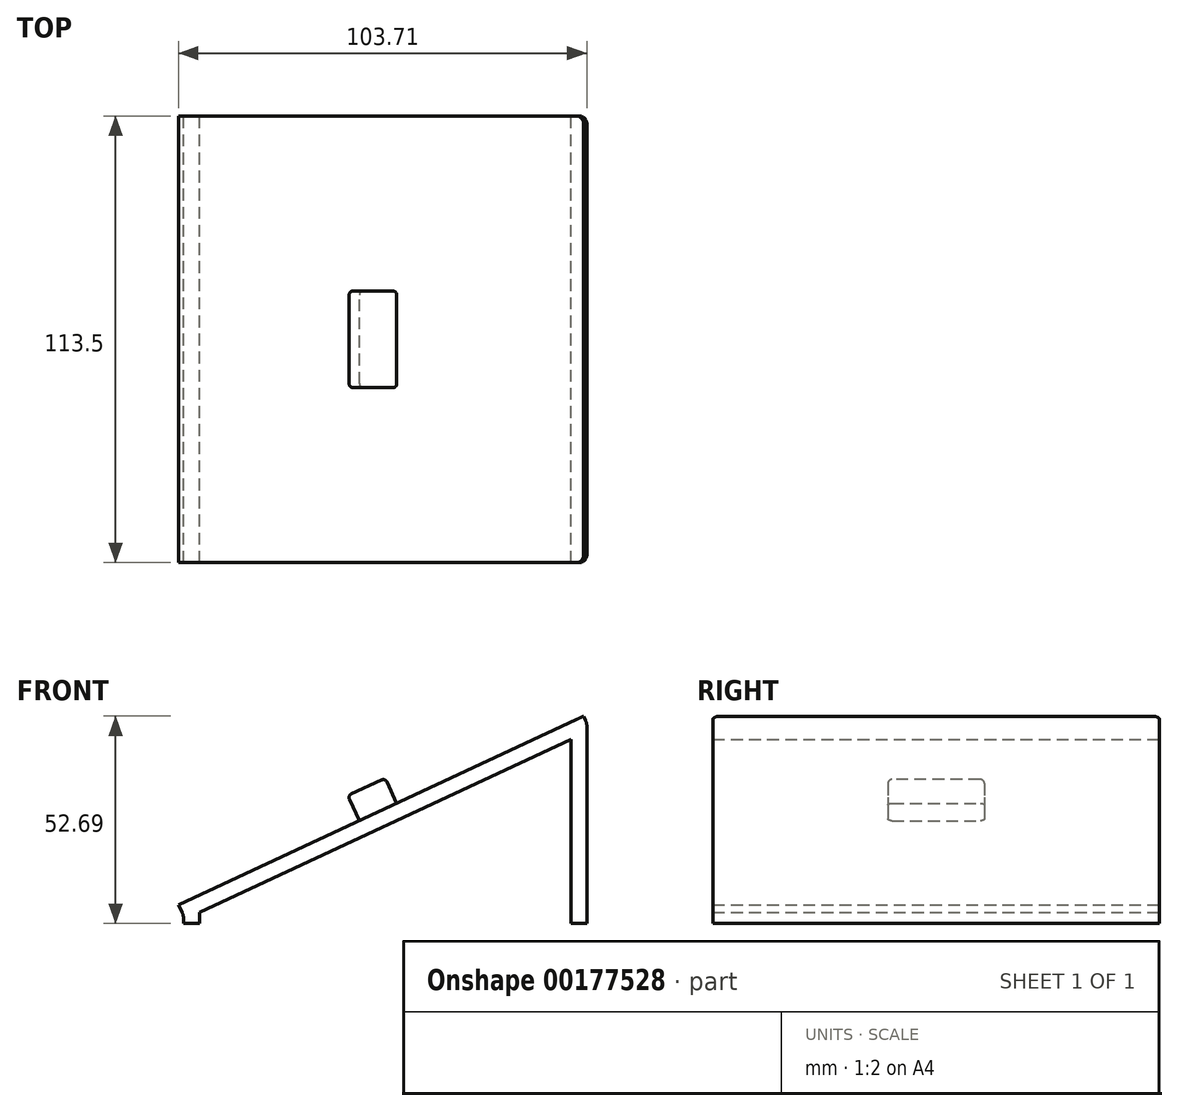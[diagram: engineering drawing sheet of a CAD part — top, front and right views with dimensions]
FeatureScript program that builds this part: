
annotation { "Feature Type Name" : "Feature", "Feature Type Description" : "" }
export const myFeature = defineFeature(function(context is Context, id is Id, definition is map)
    precondition{}
    {
        {
            var Q0;
            Q0=qCreatedBy(makeId("Front.planeOp"),FACE);
            var sketch = newSketch(context, id + "F0", { "sketchPlane" : qUnion([Q0])});
            skLineSegment(sketch, "E0", {"start": v(-51.22, 0) * mm, "end": v(51.22, 0) * mm, "construction": true});
            skLineSegment(sketch, "E1", {"start": v(51.22, 0) * mm, "end": v(51.22, 50.87) * mm});
            skLineSegment(sketch, "E2", {"start": v(-51.22, 2) * mm, "end": v(-51.22, 0) * mm});
            skLineSegment(sketch, "E3", {"start": v(-51.22, 2) * mm, "end": v(-52.49, 4.72) * mm});
            skLineSegment(sketch, "E4", {"start": v(51.22, 50.87) * mm, "end": v(50.38, 52.69) * mm});
            skLineSegment(sketch, "E5", {"start": v(-52.49, 4.72) * mm, "end": v(50.38, 52.69) * mm});
            skLineSegment(sketch, "E6.0", {"start": v(47.22, 0) * mm, "end": v(47.22, 46.8) * mm});
            skLineSegment(sketch, "E6.1", {"start": v(-47.17, 2.78) * mm, "end": v(47.22, 46.8) * mm});
            skLineSegment(sketch, "E6.2", {"start": v(-47.17, 2.78) * mm, "end": v(-47.22, 2.89) * mm});
            skLineSegment(sketch, "E6.3", {"start": v(-47.22, 2.89) * mm, "end": v(-47.22, 0) * mm});
            skLineSegment(sketch, "E7", {"start": v(-51.22, 0) * mm, "end": v(-47.22, 0) * mm});
            skLineSegment(sketch, "E8", {"start": v(47.22, 0) * mm, "end": v(51.22, 0) * mm});
            skSolve(sketch);
        }
        {
            var Q0;
            Q0=makeQuery(id+"F0.imprint","IMPRINT",FACE,{"disambiguationData":[TD([[makeQuery(id+"F0.imprint","IMPRINT",EDGE,{"derivedFrom":sQuery(id+"F0.wireOp",EDGE,"E1")}),1.0]])]});
            extrude(context, id + "F1", {"entities" : qUnion([Q0]), "depth" : 113.5 * mm, "symmetric" : true});
        }
        {
            var Q0;
            Q0=makeQuery(id+"F1.opExtrude","SWEPT_EDGE",EDGE,{"disambiguationData":[OSD([sQuery(id+"F0.wireOp",EDGE,"E1"),sQuery(id+"F0.wireOp",EDGE,"E4")])]});
            var Q1;
            Q1=makeQuery(id+"F1.opExtrude","SWEPT_EDGE",EDGE,{"disambiguationData":[OSD([sQuery(id+"F0.wireOp",EDGE,"E2"),sQuery(id+"F0.wireOp",EDGE,"E3")])]});
            fillet(context, id + "F2", {"entities" : qUnion([Q0, Q1]), "radius" : 4 * mm, "tangentPropagation" : true, "allowEdgeOverflow" : false});
        }
        {
            var Q0;
            Q0=makeQuery(id+"F1.opExtrude","SWEPT_FACE",FACE,{"disambiguationData":[OSD([sQuery(id+"F0.wireOp",EDGE,"E5")])]});
            var sketch = newSketch(context, id + "F3", { "sketchPlane" : qUnion([Q0])});
            skLineSegment(sketch, "E9", {"start": v(-46.42, 0) * mm, "end": v(67.08, 0) * mm, "construction": true});
            skPoint(sketch, "E10", {"position": v(10.33, 0) * mm});
            skLineSegment(sketch, "E11", {"start": v(10.33, 44.71) * mm, "end": v(10.33, -42.62) * mm, "construction": true});
            skLineSegment(sketch, "E12.bottom", {"start": v(14.58, -12.25) * mm, "end": v(6.08, -12.25) * mm});
            skLineSegment(sketch, "E12.top", {"start": v(14.58, 12.25) * mm, "end": v(6.08, 12.25) * mm});
            skLineSegment(sketch, "E12.left", {"start": v(15.58, -11.25) * mm, "end": v(15.58, 11.25) * mm});
            skLineSegment(sketch, "E12.right", {"start": v(5.08, -11.25) * mm, "end": v(5.08, 11.25) * mm});
            skPoint(sketch, "E13.visualSharp", {"position": v(5.08, 12.25) * mm});
            skArc(sketch, "E13.filletArc", {"start": v(6.08, 12.25) * mm, "mid": v(5.37, 11.96) * mm, "end": v(5.08, 11.25) * mm});
            skPoint(sketch, "E14.visualSharp", {"position": v(15.58, 12.25) * mm});
            skArc(sketch, "E14.filletArc", {"start": v(15.58, 11.25) * mm, "mid": v(15.28, 11.96) * mm, "end": v(14.58, 12.25) * mm});
            skPoint(sketch, "E15.visualSharp", {"position": v(15.58, -12.25) * mm});
            skArc(sketch, "E15.filletArc", {"start": v(14.58, -12.25) * mm, "mid": v(15.28, -11.96) * mm, "end": v(15.58, -11.25) * mm});
            skPoint(sketch, "E16.visualSharp", {"position": v(5.08, -12.25) * mm});
            skArc(sketch, "E16.filletArc", {"start": v(5.08, -11.25) * mm, "mid": v(5.37, -11.96) * mm, "end": v(6.08, -12.25) * mm});
            skSolve(sketch);
        }
        {
            var Q0;
            Q0=makeQuery(id+"F3.imprint","IMPRINT",FACE,{"disambiguationData":[TD([[makeQuery(id+"F3.imprint","IMPRINT",EDGE,{"derivedFrom":sQuery(id+"F3.wireOp",EDGE,"E12.bottom")}),-1.0]])]});
            extrude(context, id + "F4", {"entities" : qUnion([Q0]), "operationType" : NewBodyOperationType.ADD, "depth" : 7 * mm});
        }
        {
            var Q0;
            Q0=makeQuery(id+"F4.opExtrude","CAP_EDGE",EDGE,{"disambiguationData":[OSD([sQuery(id+"F3.wireOp",EDGE,"E12.bottom")])],"isStart":false});
            fillet(context, id + "F5", {"entities" : qUnion([Q0]), "radius" : 1 * mm, "tangentPropagation" : true, "allowEdgeOverflow" : false});
        }
        {
            var Q0;
            Q0=makeQuery(id+"F1.opExtrude","CAP_EDGE",EDGE,{"disambiguationData":[OSD([sQuery(id+"F0.wireOp",EDGE,"E1")])],"isStart":false});
            var Q1;
            Q1=makeQuery(id+"F1.opExtrude","CAP_EDGE",EDGE,{"disambiguationData":[OSD([sQuery(id+"F0.wireOp",EDGE,"E1")])],"isStart":true});
            fillet(context, id + "F6", {"entities" : qUnion([Q0, Q1]), "radius" : 2 * mm, "tangentPropagation" : true, "allowEdgeOverflow" : false});
        }
    });
